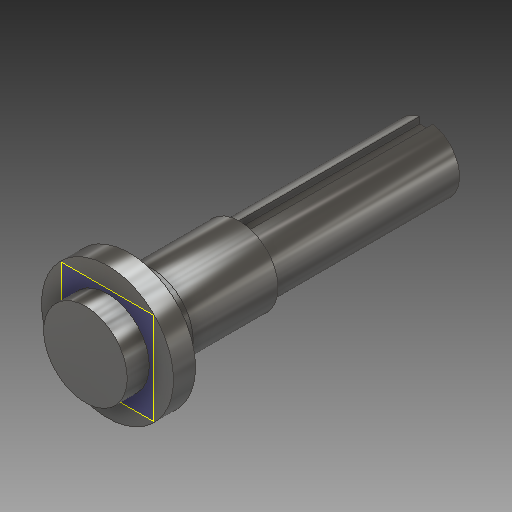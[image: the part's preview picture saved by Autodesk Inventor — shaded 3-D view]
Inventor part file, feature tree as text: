
AUTODESK INVENTOR PART (.ipt)
format: ipt  version: 2019 (Build 230136000, 136)  size: 159,744 bytes
history: native  units: in
note: dims shown in document units (in); Inventor stores cm internally (conversion verified against a paired STEP export)
features: sketch x5, other x3, plane x1
ambient origin geometry x8: Origin, YZ Plane, XZ Plane, XY Plane, X Axis, Y Axis, Z Axis, Center Point
bodies: Solid1 (feature_tree)
feature tree (9):
  other  "project handle part(1).ipt"
  other  "Solid1::project handle part(1).ipt"
  other  "TaggingFeature1"
  sketch  "Sketch1"  dims[d0=0.3937in]
  sketch  "Sketch2"
  sketch  "Sketch3"
  sketch  "Sketch4"
  sketch  "Sketch5"
  plane  "Work Plane1"
